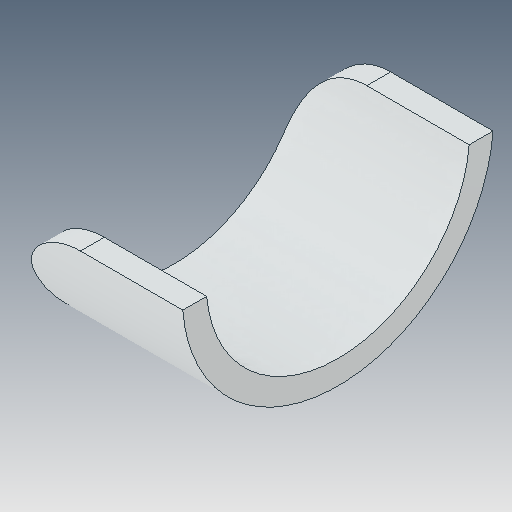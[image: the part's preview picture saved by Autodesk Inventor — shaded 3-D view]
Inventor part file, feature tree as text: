
AUTODESK INVENTOR PART (.ipt)
format: ipt  version: 2023.5 (Build 275446000, 446)  size: 112,128 bytes
history: native  units: in
note: dims shown in document units (in); Inventor stores cm internally (conversion verified against a paired STEP export)
features: fillet x1
ambient origin geometry x8: Origin, YZ Plane, XZ Plane, XY Plane, X Axis, Y Axis, Z Axis, Center Point
bodies: Solid1 (feature_tree)
feature tree (1):
  fillet  "Fillet1"  [1 undecoded]
note: 1 required parameter value undecoded (feature->parameter linkage not recoverable at this tier; creation-order binding heuristic only, values carry confidence <= 0.55)
